# Revit family: Gira_2003600
name_source: partatom
category: Electrical Fixtures
revit_build: Autodesk Revit 2017 (Build: 20160225_1515(x64)
units: mm (PartAtom-declared; Revit-internal decimal feet)

## family parameters
Cut with Voids When Loaded = No
Host = Face
Maintain Annotation Orientation = Yes
Part Type = Normal
Room Calculation Point = No
Round Connector Dimension = Use Diameter
Shared = No

## types (1)
- PB sens.2 3-g 24 V zero-volt. in.sp. System 55 stainl.steel
    BIM = https://media.live.bim.site und Tasten.rfa
    BIMSITE_PRODUCT_ID = c37665e588a4d1d6b732b5195e1232502ac65da8
    Bus connection included = No
    Colour = Stainless steel
    Cost = 0 $
    Default Elevation = 1219 mm
    Description = PB sens.2 3g 24V z-v in.sp. Sys55 SST Pushbutton sensor 2, 3-gang 24 V zero-voltage with inscription space,Stainless steel Features: Pushbutton sensor 2 for connection to 24 V control systems: - Three rockers with two red LEDs each for status display. - Disassembly safeguard by screw connection. - Backlighting. - Connection of six buttons, six LEDs, and backlighting via the terminal block on the rear.,Notes : - Suitable for SELV circuits only. - Can also be connected with illumination. - Professional labelling with the Gira Inscription Service www.marking.gira.com.
    GTIN = 4010337020363
    HAN = 2003600
    HeinzeBIM = https://www.heinze.de
    Manufacturer = Gira
    Material = Sonstige (*de-DE)
    Material quality = Sonstige (*de-DE)
    Number of actuation points = 6
    Number of buttons = 3
    Surface finishing = Not applicable
    Surface protection = Lacquered
    Transparent = No
    URL = https://www.gira.de
    With IR sensor = No
    With anti-theft/dismantling protection = No
    With display = No
    With label area = Yes
    With room temperature controller = No

## geometry (parser evidence)
native form markers: Blend x2, Sweep x10
no freeform markers — native parametric forms only
